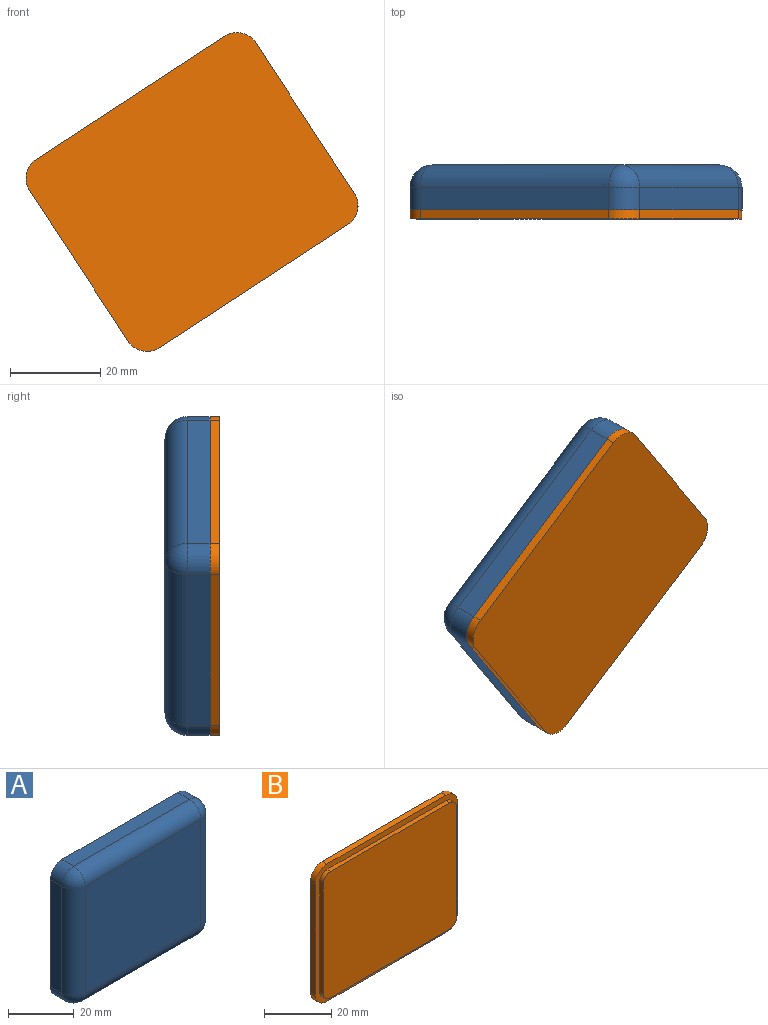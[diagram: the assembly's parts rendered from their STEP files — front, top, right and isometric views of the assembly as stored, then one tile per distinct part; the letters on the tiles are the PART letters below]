
ASSEMBLY  parts=2 mates=1
PART A: 35 faces, bbox 60x10x50 mm
  f0: plane 60x50mm, normal (0,1,0), area 310.1mm2, adj f1,f2,f3,f4,f6,f8,f11,f17
  f1: plane 40x5mm, normal (-1,0,0), area 200mm2, adj f0,f8,f14,f17
  f2: plane 50x5mm, normal (0,0,-1), area 250mm2, adj f0,f11,f15,f17
  f3: plane 40x5mm, normal (1,0,0), area 200mm2, adj f0,f6,f10,f11
  f4: plane 50x5mm, normal (0,0,1), area 250mm2, adj f0,f6,f8,f9
  f5: plane 50x40mm, normal (0,-1,0), area 2000mm2, adj f9,f10,f14,f15
  f6: cylinder r=5mm len=5mm, axis (0,1,0), area 39.3mm2, adj f0,f3,f4,f7
  f7: sphere r=5mm, area 39.3mm2, adj f6,f9,f10
  f8: cylinder r=5mm len=5mm, axis (0,-1,0), area 39.3mm2, adj f0,f1,f4,f12
  f9: cylinder r=5mm len=50mm, axis (1,0,0), area 392.7mm2, adj f4,f5,f7,f12
  f10: cylinder r=5mm len=40mm, axis (0,0,-1), area 314.2mm2, adj f3,f5,f7,f13
  f11: cylinder r=5mm len=5mm, axis (0,-1,0), area 39.3mm2, adj f0,f2,f3,f13
  f12: sphere r=5mm, area 39.3mm2, adj f8,f9,f14
  f13: sphere r=5mm, area 39.3mm2, adj f10,f11,f15
  f14: cylinder r=5mm len=40mm, axis (0,0,1), area 314.2mm2, adj f1,f5,f12,f16
  f15: cylinder r=5mm len=50mm, axis (-1,0,0), area 392.7mm2, adj f2,f5,f13,f16
  f16: sphere r=5mm, area 39.3mm2, adj f14,f15,f17
  f17: cylinder r=5mm len=5mm, axis (0,1,0), area 39.3mm2, adj f0,f1,f2,f16
  f18: plane 40x5mm, normal (1,0,0), area 200mm2, adj f0,f25,f31,f34
  f19: plane 50x5mm, normal (0,0,1), area 250mm2, adj f0,f28,f32,f34
  f20: plane 40x5mm, normal (-1,0,0), area 200mm2, adj f0,f23,f27,f28
  f21: plane 50x5mm, normal (0,0,-1), area 250mm2, adj f0,f23,f25,f26
  f22: plane 50x40mm, normal (0,1,0), area 2000mm2, adj f26,f27,f31,f32
  f23: cylinder r=3.5mm len=5mm, axis (0,1,0), area 27.5mm2, adj f0,f20,f21,f24
  f24: sphere r=3.5mm, area 19.2mm2, adj f23,f26,f27
  f25: cylinder r=3.5mm len=5mm, axis (0,-1,0), area 27.5mm2, adj f0,f18,f21,f29
  f26: cylinder r=3.5mm len=50mm, axis (1,0,0), area 274.9mm2, adj f21,f22,f24,f29
  f27: cylinder r=3.5mm len=40mm, axis (0,0,-1), area 219.9mm2, adj f20,f22,f24,f30
  f28: cylinder r=3.5mm len=5mm, axis (0,-1,0), area 27.5mm2, adj f0,f19,f20,f30
  f29: sphere r=3.5mm, area 19.2mm2, adj f25,f26,f31
  f30: sphere r=3.5mm, area 19.2mm2, adj f27,f28,f32
  f31: cylinder r=3.5mm len=40mm, axis (0,0,1), area 219.9mm2, adj f18,f22,f29,f33
  f32: cylinder r=3.5mm len=50mm, axis (-1,0,0), area 274.9mm2, adj f19,f22,f30,f33
  f33: sphere r=3.5mm, area 19.2mm2, adj f31,f32,f34
  f34: cylinder r=3.5mm len=5mm, axis (0,1,0), area 27.5mm2, adj f0,f18,f19,f33
PART B: 19 faces, bbox 60x3.5x50 mm
  f0: plane 40x2mm, normal (1,0,0), area 80mm2, adj f4,f5,f11,f14
  f1: plane 50x2mm, normal (0,0,1), area 100mm2, adj f4,f5,f11,f12
  f2: plane 40x2mm, normal (-1,0,0), area 80mm2, adj f4,f5,f12,f13
  f3: plane 50x2mm, normal (0,0,-1), area 100mm2, adj f4,f5,f13,f14
  f4: plane 60x50mm, normal (0,-1,0), area 410.3mm2, adj f0,f1,f2,f3,f6,f7,f8,f9
  f5: plane 60x50mm, normal (0,1,0), area 2978.5mm2, adj f0,f1,f2,f3,f11,f12,f13,f14
  f6: plane 40x1.5mm, normal (-1,0,0), area 60mm2, adj f4,f10,f15,f18
  f7: plane 50x1.5mm, normal (0,0,-1), area 75mm2, adj f4,f10,f15,f16
  f8: plane 40x1.5mm, normal (1,0,0), area 60mm2, adj f4,f10,f16,f17
  f9: plane 50x1.5mm, normal (0,0,1), area 75mm2, adj f4,f10,f17,f18
  f10: plane 56x46mm, normal (0,-1,0), area 2568.3mm2, adj f6,f7,f8,f9,f15,f16,f17,f18
  f11: cylinder r=5mm len=5mm, axis (0,1,0), area 15.7mm2, adj f0,f1,f4,f5
  f12: cylinder r=5mm len=5mm, axis (0,-1,0), area 15.7mm2, adj f1,f2,f4,f5
  f13: cylinder r=5mm len=5mm, axis (0,1,0), area 15.7mm2, adj f2,f3,f4,f5
  f14: cylinder r=5mm len=5mm, axis (0,-1,0), area 15.7mm2, adj f0,f3,f4,f5
  f15: cylinder r=3mm len=3mm, axis (0,1,0), area 7.1mm2, adj f4,f6,f7,f10
  f16: cylinder r=3mm len=3mm, axis (0,-1,0), area 7.1mm2, adj f4,f7,f8,f10
  f17: cylinder r=3mm len=3mm, axis (0,1,0), area 7.1mm2, adj f4,f8,f9,f10
  f18: cylinder r=3mm len=3mm, axis (0,-1,0), area 7.1mm2, adj f4,f6,f9,f10
PLACE A rot(axis=(0.29,0,-0.96),180deg) t=(-71.16,-20.63,-7.33)mm
PLACE B rot(axis=(0.29,0,-0.96),180deg) t=(-71.16,-22.63,-7.33)mm
MATE parallel B.f3 <-> A.f2  axis (0.55,0,-0.84) through (-46.04,-21.63,9.08)mm
